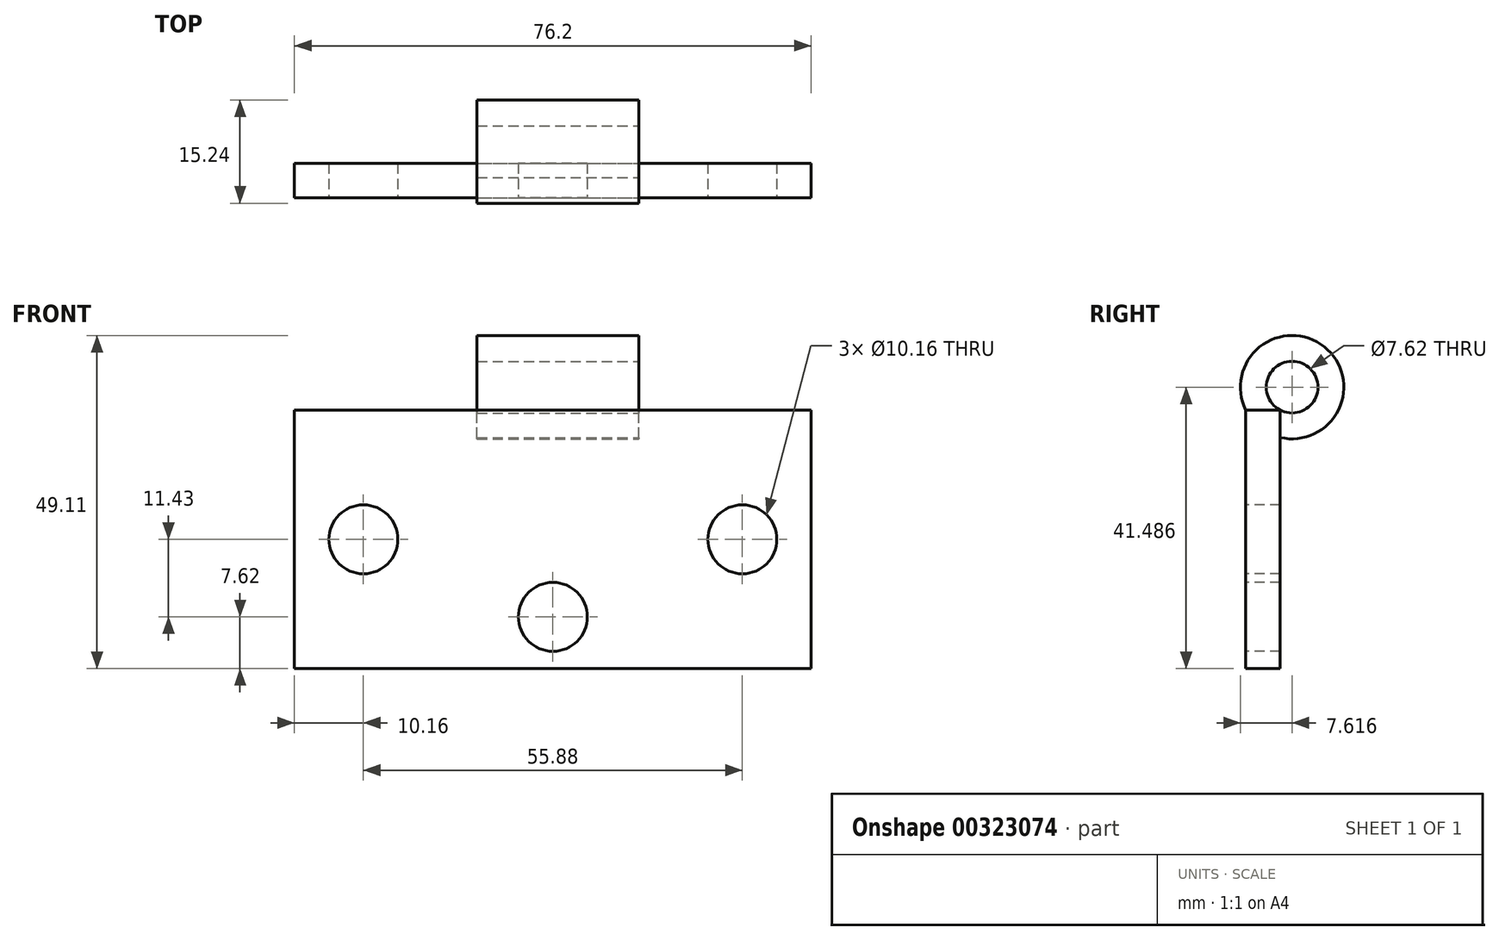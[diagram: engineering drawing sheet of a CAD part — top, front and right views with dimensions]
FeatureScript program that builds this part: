
annotation { "Feature Type Name" : "Feature", "Feature Type Description" : "" }
export const myFeature = defineFeature(function(context is Context, id is Id, definition is map)
    precondition{}
    {
        {
            var Q0;
            Q0=qCreatedBy(makeId("Front.planeOp"),FACE);
            var sketch = newSketch(context, id + "F0", { "sketchPlane" : qUnion([Q0])});
            skLineSegment(sketch, "E0.bottom", {"start": v(-38.1, 19.05) * mm, "end": v(38.1, 19.05) * mm});
            skLineSegment(sketch, "E0.top", {"start": v(-38.1, -19.05) * mm, "end": v(38.1, -19.05) * mm});
            skLineSegment(sketch, "E0.left", {"start": v(-38.1, 19.05) * mm, "end": v(-38.1, -19.05) * mm});
            skLineSegment(sketch, "E0.right", {"start": v(38.1, 19.05) * mm, "end": v(38.1, -19.05) * mm});
            skSolve(sketch);
        }
        {
            var Q0;
            Q0 = qSketchRegion(id + "F0", true);
            extrude(context, id + "F1", {"entities" : qUnion([Q0]), "depth" : 5.08 * mm});
        }
        {
            var Q0;
            Q0=makeQuery(id+"F1.opExtrude","SWEPT_FACE",FACE,{"disambiguationData":[OSD([sQuery(id+"F0.wireOp",EDGE,"E0.right")])]});
            var sketch = newSketch(context, id + "F2", { "sketchPlane" : qUnion([Q0])});
            skCircle(sketch, "E1", {"center": v(1.75, 22.44) * mm, "radius": 7.62 * mm});
            skCircle(sketch, "E2", {"center": v(1.75, 22.44) * mm, "radius": 3.81 * mm});
            skSolve(sketch);
        }
        {
            var Q0;
            Q0 = qSketchRegion(id + "F2", true);
            extrude(context, id + "F3", {"entities" : qUnion([Q0]), "operationType" : NewBodyOperationType.ADD, "oppositeDirection" : true, "depth" : 49.28 * mm, "hasSecondDirection" : true, "secondDirectionOppositeDirection" : true, "secondDirectionDepth" : 25.4 * mm});
        }
        {
            var Q0;
            Q0=makeQuery(id+"F1.opExtrude","CAP_FACE",FACE,{"disambiguationData":[OSD([sQuery(id+"F0.wireOp",EDGE,"E0.bottom"),sQuery(id+"F0.wireOp",EDGE,"E0.top"),sQuery(id+"F0.wireOp",EDGE,"E0.left"),sQuery(id+"F0.wireOp",EDGE,"E0.right")])],"isStart":false});
            var sketch = newSketch(context, id + "F4", { "sketchPlane" : qUnion([Q0])});
            skCircle(sketch, "E3", {"center": v(-27.94, 0) * mm, "radius": 5.08 * mm});
            skCircle(sketch, "E4", {"center": v(0, -11.43) * mm, "radius": 5.08 * mm});
            skCircle(sketch, "E5", {"center": v(27.94, 0) * mm, "radius": 5.08 * mm});
            skSolve(sketch);
        }
        {
            var Q0;
            Q0 = qSketchRegion(id + "F4", true);
            extrude(context, id + "F5", {"entities" : qUnion([Q0]), "operationType" : NewBodyOperationType.REMOVE, "endBound" : BoundingType.UP_TO_NEXT, "oppositeDirection" : true, "depth" : 25.4 * mm});
        }
    });
